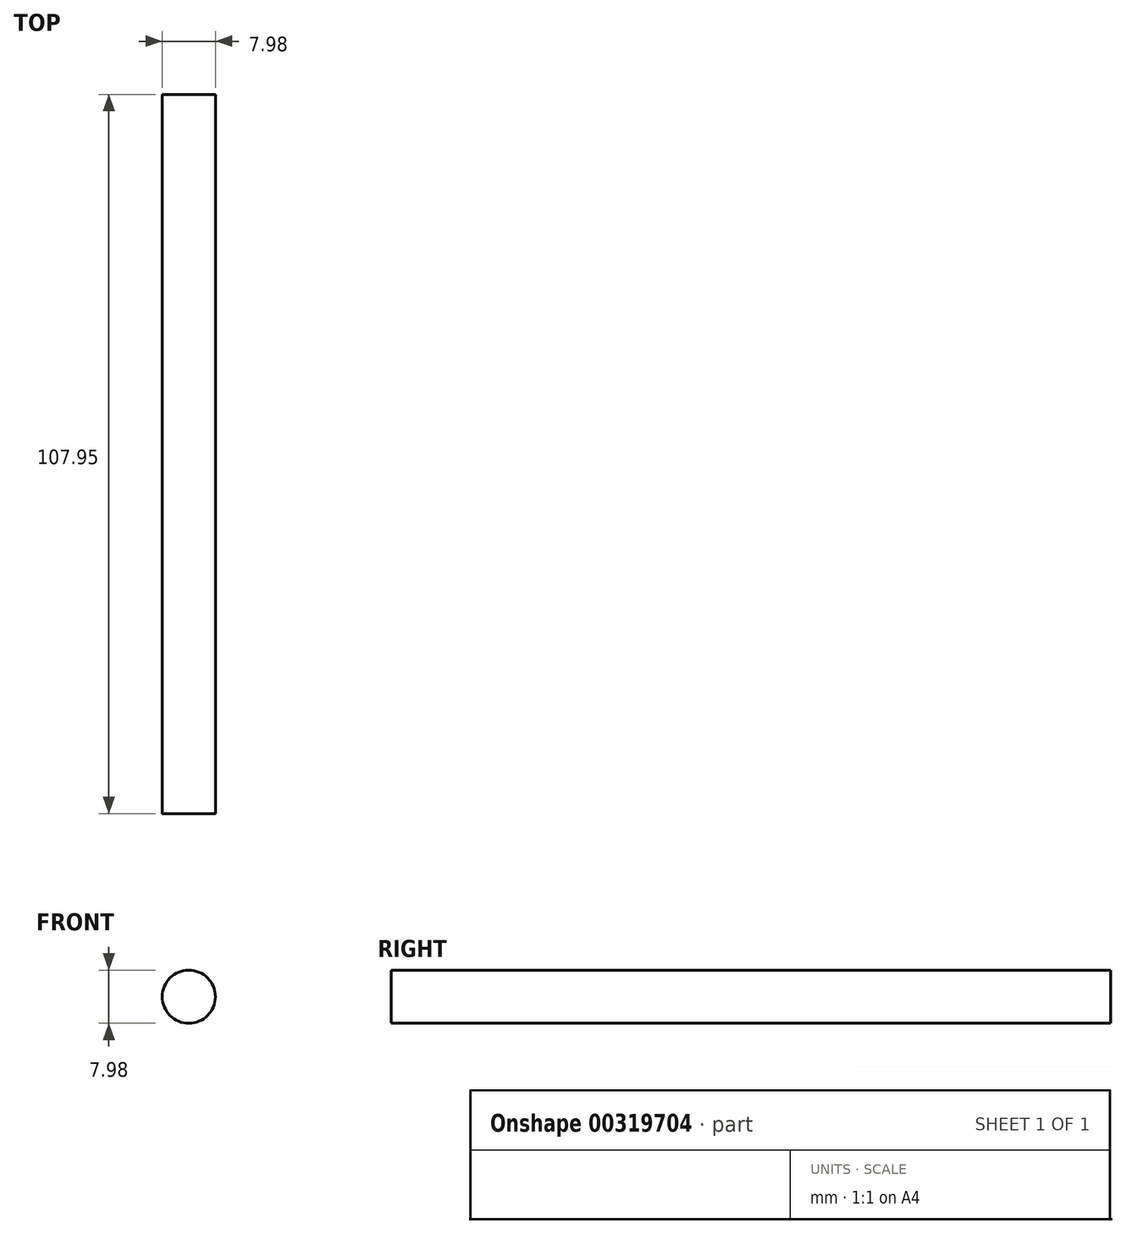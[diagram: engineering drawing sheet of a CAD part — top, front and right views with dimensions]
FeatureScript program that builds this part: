
annotation { "Feature Type Name" : "Feature", "Feature Type Description" : "" }
export const myFeature = defineFeature(function(context is Context, id is Id, definition is map)
    precondition{}
    {
        {
            var Q0;
            Q0=qCreatedBy(makeId("Front.planeOp"),FACE);
            var sketch = newSketch(context, id + "F0", { "sketchPlane" : qUnion([Q0])});
            skCircle(sketch, "E0", {"center": v(0, 0) * mm, "radius": 3.99 * mm});
            skSolve(sketch);
        }
        {
            var Q0;
            Q0=makeQuery(id+"F0.imprint","IMPRINT",FACE,{"disambiguationData":[TD([[makeQuery(id+"F0.imprint","IMPRINT",EDGE,{"derivedFrom":sQuery(id+"F0.wireOp",EDGE,"E0")}),1.0]])]});
            extrude(context, id + "F1", {"entities" : qUnion([Q0]), "depth" : 107.95 * mm});
        }
    });
